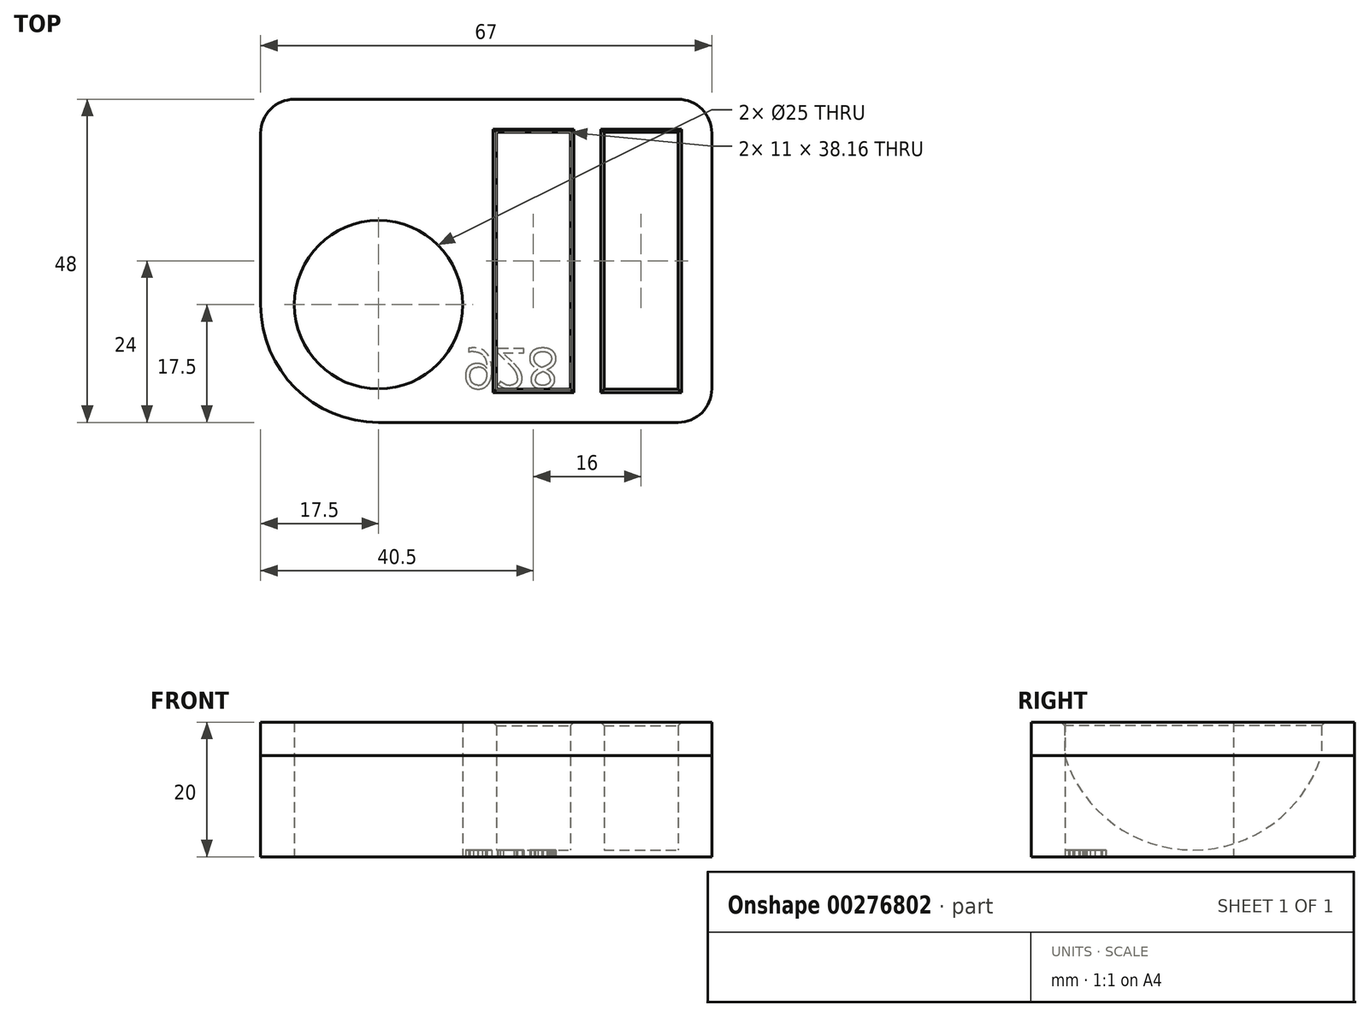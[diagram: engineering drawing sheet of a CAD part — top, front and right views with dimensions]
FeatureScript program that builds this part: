
annotation { "Feature Type Name" : "Feature", "Feature Type Description" : "" }
export const myFeature = defineFeature(function(context is Context, id is Id, definition is map)
    precondition{}
    {
        {
            var Q0;
            Q0=qCreatedBy(makeId("Top.planeOp"),FACE);
            var sketch = newSketch(context, id + "F0", { "sketchPlane" : qUnion([Q0])});
            skLineSegment(sketch, "E0.bottom", {"start": v(17.5, 0) * mm, "end": v(62, 0) * mm});
            skLineSegment(sketch, "E0.top", {"start": v(5, 48) * mm, "end": v(62, 48) * mm});
            skLineSegment(sketch, "E0.left", {"start": v(0, 17.5) * mm, "end": v(0, 43) * mm});
            skLineSegment(sketch, "E0.right", {"start": v(67, 5) * mm, "end": v(67, 43) * mm});
            skLineSegment(sketch, "E1.bottom", {"start": v(0, 0) * mm, "end": v(17.5, 0) * mm, "construction": true});
            skLineSegment(sketch, "E1.top", {"start": v(0, 17.5) * mm, "end": v(17.5, 17.5) * mm, "construction": true});
            skLineSegment(sketch, "E1.left", {"start": v(0, 0) * mm, "end": v(0, 17.5) * mm, "construction": true});
            skLineSegment(sketch, "E1.right", {"start": v(17.5, 0) * mm, "end": v(17.5, 17.5) * mm, "construction": true});
            skCircle(sketch, "E2", {"center": v(17.5, 17.5) * mm, "radius": 12.5 * mm});
            skPoint(sketch, "E3.visualSharp", {"position": v(0, 0) * mm});
            skArc(sketch, "E3.filletArc", {"start": v(0, 17.5) * mm, "mid": v(5.13, 5.13) * mm, "end": v(17.5, 0) * mm});
            skPoint(sketch, "E4.visualSharp", {"position": v(0, 48) * mm});
            skArc(sketch, "E4.filletArc", {"start": v(5, 48) * mm, "mid": v(1.46, 46.54) * mm, "end": v(0, 43) * mm});
            skPoint(sketch, "E5.visualSharp", {"position": v(67, 48) * mm});
            skArc(sketch, "E5.filletArc", {"start": v(67, 43) * mm, "mid": v(65.54, 46.54) * mm, "end": v(62, 48) * mm});
            skPoint(sketch, "E6.visualSharp", {"position": v(67, 0) * mm});
            skArc(sketch, "E6.filletArc", {"start": v(62, 0) * mm, "mid": v(65.54, 1.46) * mm, "end": v(67, 5) * mm});
            skSolve(sketch);
        }
        {
            var Q0;
            Q0=makeQuery(id+"F0.imprint","IMPRINT",FACE,{"disambiguationData":[TD([[makeQuery(id+"F0.imprint","IMPRINT",EDGE,{"derivedFrom":sQuery(id+"F0.wireOp",EDGE,"E0.bottom")}),1.0]])]});
            extrude(context, id + "F1", {"entities" : qUnion([Q0]), "depth" : 21 * mm});
        }
        {
            var Q0;
            Q0=makeQuery(id+"F1.opExtrude","CAP_FACE",FACE,{"disambiguationData":[OSD([sQuery(id+"F0.wireOp",EDGE,"E0.bottom"),sQuery(id+"F0.wireOp",EDGE,"E0.top"),sQuery(id+"F0.wireOp",EDGE,"E0.right"),sQuery(id+"F0.wireOp",EDGE,"E2"),sQuery(id+"F0.wireOp",EDGE,"E3.filletArc"),sQuery(id+"F0.wireOp",EDGE,"E4.filletArc"),sQuery(id+"F0.wireOp",EDGE,"E5.filletArc"),sQuery(id+"F0.wireOp",EDGE,"E6.filletArc")])],"isStart":false});
            var sketch = newSketch(context, id + "F2", { "sketchPlane" : qUnion([Q0])});
            skLineSegment(sketch, "E7.bottom", {"start": v(0, 0) * mm, "end": v(35, 0) * mm, "construction": true});
            skLineSegment(sketch, "E7.top", {"start": v(0, 24) * mm, "end": v(35, 24) * mm, "construction": true});
            skLineSegment(sketch, "E7.left", {"start": v(0, 0) * mm, "end": v(0, 24) * mm, "construction": true});
            skLineSegment(sketch, "E7.right", {"start": v(35, 0) * mm, "end": v(35, 24) * mm, "construction": true});
            skLineSegment(sketch, "E8.bottom", {"start": v(35, 24) * mm, "end": v(46, 24) * mm});
            skLineSegment(sketch, "E8.top", {"start": v(35, 4) * mm, "end": v(46, 4) * mm});
            skLineSegment(sketch, "E8.left", {"start": v(35, 24) * mm, "end": v(35, 4) * mm});
            skLineSegment(sketch, "E8.right", {"start": v(46, 24) * mm, "end": v(46, 4) * mm});
            skLineSegment(sketch, "E9", {"start": v(46, 24) * mm, "end": v(51, 24) * mm, "construction": true});
            skLineSegment(sketch, "E10.bottom", {"start": v(51, 24) * mm, "end": v(62, 24) * mm});
            skLineSegment(sketch, "E10.top", {"start": v(51, 4) * mm, "end": v(62, 4) * mm});
            skLineSegment(sketch, "E10.left", {"start": v(51, 24) * mm, "end": v(51, 4) * mm});
            skLineSegment(sketch, "E10.right", {"start": v(62, 24) * mm, "end": v(62, 4) * mm});
            skSolve(sketch);
        }
        {
            var Q0;
            Q0=makeQuery(id+"F2.imprint","IMPRINT",FACE,{"disambiguationData":[TD([[makeQuery(id+"F2.imprint","IMPRINT",EDGE,{"derivedFrom":sQuery(id+"F2.wireOp",EDGE,"E8.bottom")}),-1.0]])]});
            var Q1;
            Q1=makeQuery(id+"F2.imprint","IMPRINT",FACE,{"disambiguationData":[TD([[makeQuery(id+"F2.imprint","IMPRINT",EDGE,{"derivedFrom":sQuery(id+"F2.wireOp",EDGE,"E10.bottom")}),-1.0]])]});
            var Q2;
            Q2=sQuery(id+"F2.wireOp",EDGE,"E8.bottom");
            revolve(context, id + "F3", {"operationType" : NewBodyOperationType.REMOVE, "entities" : qUnion([Q0, Q1]), "axis" : qUnion([Q2]), "revolveType" : RevolveType.FULL, "oppositeDirection" : true});
        }
        {
            var Q0;
            Q0=makeQuery(id+"F1.opExtrude","SWEPT_FACE",FACE,{"disambiguationData":[OSD([sQuery(id+"F0.wireOp",EDGE,"E0.bottom")])]});
            var sketch = newSketch(context, id + "F4", { "sketchPlane" : qUnion([Q0])});
            skLineSegment(sketch, "E11", {"start": v(0, 0) * mm, "end": v(0, 15) * mm, "construction": true});
            skLineSegment(sketch, "E12.bottom", {"start": v(0, 15) * mm, "end": v(83.8, 15) * mm});
            skLineSegment(sketch, "E12.top", {"start": v(0, 25.63) * mm, "end": v(83.8, 25.63) * mm});
            skLineSegment(sketch, "E12.left", {"start": v(0, 15) * mm, "end": v(0, 25.63) * mm});
            skLineSegment(sketch, "E12.right", {"start": v(83.8, 15) * mm, "end": v(83.8, 25.63) * mm});
            skSolve(sketch);
        }
        {
            var Q0;
            Q0=qSketchRegion(id+"F4",true);
            extrude(context, id + "F5", {"entities" : qUnion([Q0]), "operationType" : NewBodyOperationType.REMOVE, "endBound" : BoundingType.THROUGH_ALL, "oppositeDirection" : true, "depth" : 25 * mm});
        }
        {
            var Q0;
            Q0=makeQuery(id+"F1.opExtrude","CAP_FACE",FACE,{"disambiguationData":[OSD([sQuery(id+"F0.wireOp",EDGE,"E0.bottom"),sQuery(id+"F0.wireOp",EDGE,"E0.top"),sQuery(id+"F0.wireOp",EDGE,"E0.left"),sQuery(id+"F0.wireOp",EDGE,"E0.right"),sQuery(id+"F0.wireOp",EDGE,"E2"),sQuery(id+"F0.wireOp",EDGE,"E3.filletArc"),sQuery(id+"F0.wireOp",EDGE,"E4.filletArc"),sQuery(id+"F0.wireOp",EDGE,"E5.filletArc"),sQuery(id+"F0.wireOp",EDGE,"E6.filletArc")])],"isStart":true});
            var sketch = newSketch(context, id + "F6", { "sketchPlane" : qUnion([Q0])});
            skLineSegment(sketch, "E13.bottom", {"start": v(0, 0) * mm, "end": v(30, 0) * mm, "construction": true});
            skLineSegment(sketch, "E13.top", {"start": v(0, -5) * mm, "end": v(30, -5) * mm, "construction": true});
            skLineSegment(sketch, "E13.left", {"start": v(0, 0) * mm, "end": v(0, -5) * mm, "construction": true});
            skLineSegment(sketch, "E13.right", {"start": v(30, 0) * mm, "end": v(30, -5) * mm, "construction": true});
            skText(sketch, "E14", { "text": "928", "fontName": "OpenSans-Regular.ttf"});
            const initialGuessF6  = {"E14": [0.03, -0.011, 1, 0, 0.006]};
            skSetInitialGuess(sketch, initialGuessF6);
            skSolve(sketch);
        }
        {
            var Q0;
            Q0 = qSketchRegion(id + "F6", true);
            extrude(context, id + "F7", {"entities" : qUnion([Q0]), "operationType" : NewBodyOperationType.REMOVE, "oppositeDirection" : true, "depth" : 1 * mm});
        }
        {
            var Q0;
            Q0=makeQuery(id+"F5.boolean.opBoolean","COPY",FACE,{"derivedFrom":makeQuery(id+"F5.opExtrude","SWEPT_FACE",FACE,{"disambiguationData":[OSD([sQuery(id+"F4.wireOp",EDGE,"E12.bottom")])]})});
            var sketch = newSketch(context, id + "F8", { "sketchPlane" : qUnion([Q0])});
            skCircle(sketch, "E15.0", {"center": v(17.5, 17.5) * mm, "radius": 12.5 * mm});
            skLineSegment(sketch, "E16.0", {"start": v(35, 4.92) * mm, "end": v(35, 43.08) * mm});
            skLineSegment(sketch, "E17.0", {"start": v(46, 4.92) * mm, "end": v(35, 4.92) * mm});
            skLineSegment(sketch, "E18.0", {"start": v(46, 4.92) * mm, "end": v(46, 43.08) * mm});
            skLineSegment(sketch, "E19.0", {"start": v(35, 43.08) * mm, "end": v(46, 43.08) * mm});
            skLineSegment(sketch, "E20.0", {"start": v(51, 4.92) * mm, "end": v(51, 43.08) * mm});
            skLineSegment(sketch, "E21.0", {"start": v(51, 43.08) * mm, "end": v(62, 43.08) * mm});
            skLineSegment(sketch, "E22.0", {"start": v(62, 4.92) * mm, "end": v(62, 43.08) * mm});
            skLineSegment(sketch, "E23.0", {"start": v(62, 4.92) * mm, "end": v(51, 4.92) * mm});
            skLineSegment(sketch, "E24.0", {"start": v(17.5, 0) * mm, "end": v(62, 0) * mm});
            skArc(sketch, "E25.0", {"start": v(17.5, 0) * mm, "mid": v(5.13, 5.13) * mm, "end": v(0, 17.5) * mm});
            skLineSegment(sketch, "E26.0", {"start": v(0, 43) * mm, "end": v(0, 17.5) * mm});
            skArc(sketch, "E27.0", {"start": v(0, 43) * mm, "mid": v(1.46, 46.54) * mm, "end": v(5, 48) * mm});
            skLineSegment(sketch, "E28.0", {"start": v(62, 48) * mm, "end": v(5, 48) * mm});
            skArc(sketch, "E29.0", {"start": v(62, 48) * mm, "mid": v(65.54, 46.54) * mm, "end": v(67, 43) * mm});
            skLineSegment(sketch, "E30.0", {"start": v(67, 43) * mm, "end": v(67, 5) * mm});
            skArc(sketch, "E31.0", {"start": v(67, 5) * mm, "mid": v(65.54, 1.46) * mm, "end": v(62, 0) * mm});
            skSolve(sketch);
        }
        {
            var Q0;
            Q0 = qSketchRegion(id + "F8", true);
            extrude(context, id + "F9", {"entities" : qUnion([Q0]), "depth" : 5 * mm, "offsetDistance" : 25 * mm});
        }
        {
            var Q0;
            Q0=makeQuery(id+"F9.opExtrude","CAP_EDGE",EDGE,{"disambiguationData":[OSD([sQuery(id+"F8.wireOp",EDGE,"E22.0")])],"isStart":false});
            var Q1;
            Q1=makeQuery(id+"F9.opExtrude","CAP_EDGE",EDGE,{"disambiguationData":[OSD([sQuery(id+"F8.wireOp",EDGE,"E23.0")])],"isStart":false});
            var Q2;
            Q2=makeQuery(id+"F9.opExtrude","CAP_EDGE",EDGE,{"disambiguationData":[OSD([sQuery(id+"F8.wireOp",EDGE,"E20.0")])],"isStart":false});
            var Q3;
            Q3=makeQuery(id+"F9.opExtrude","CAP_EDGE",EDGE,{"disambiguationData":[OSD([sQuery(id+"F8.wireOp",EDGE,"E17.0")])],"isStart":false});
            var Q4;
            Q4=makeQuery(id+"F9.opExtrude","CAP_EDGE",EDGE,{"disambiguationData":[OSD([sQuery(id+"F8.wireOp",EDGE,"E16.0")])],"isStart":false});
            var Q5;
            Q5=makeQuery(id+"F9.opExtrude","CAP_EDGE",EDGE,{"disambiguationData":[OSD([sQuery(id+"F8.wireOp",EDGE,"E18.0")])],"isStart":false});
            var Q6;
            Q6=makeQuery(id+"F9.opExtrude","CAP_EDGE",EDGE,{"disambiguationData":[OSD([sQuery(id+"F8.wireOp",EDGE,"E19.0")])],"isStart":false});
            var Q7;
            Q7=makeQuery(id+"F9.opExtrude","CAP_EDGE",EDGE,{"disambiguationData":[OSD([sQuery(id+"F8.wireOp",EDGE,"E21.0")])],"isStart":false});
            chamfer(context, id + "F10", {"entities" : qUnion([Q0, Q1, Q2, Q3, Q4, Q5, Q6, Q7]), "width" : .5 * mm, "tangentPropagation" : true});
        }
    });
